# Revit family: BuzziPleat - Suspended - No Light
name_source: partatom
category: Lighting Fixtures
revit_build: Autodesk Revit 2018 (Build: 20190510_1515(x64)
units: mm (PartAtom-declared; Revit-internal decimal feet)

## family parameters
Always vertical = Yes
Cut with Voids When Loaded = No
Host = Ceiling
Light Source = No
OmniClass Number = 23.80.70.11
OmniClass Title = Luminaries for Internal Lighting
Part Type = Normal
Room Calculation Point = No
Round Connector Dimension = Use Diameter
Shared = No

## types (4) — shared parameters
BuzziPleat Ripple Shade = <By Category>
Drop From Ceiling = 3' - 0"

## per-type parameters (varying)
| type | Wires |
| BuzziPleat Edel 150cm | <By Category> |
| BuzziPleat Edel 100cm | Default |
| BuzziPleat Ripple 100cm | <By Category> |
| BuzziPleat Ripple 150cm | <By Category> |

type visibility flags: 4 boolean params named "<type name>" — each type sets only its own to Yes (folded from table)

## geometry (parser evidence)
native form markers: Sweep x10
no freeform markers — native parametric forms only
